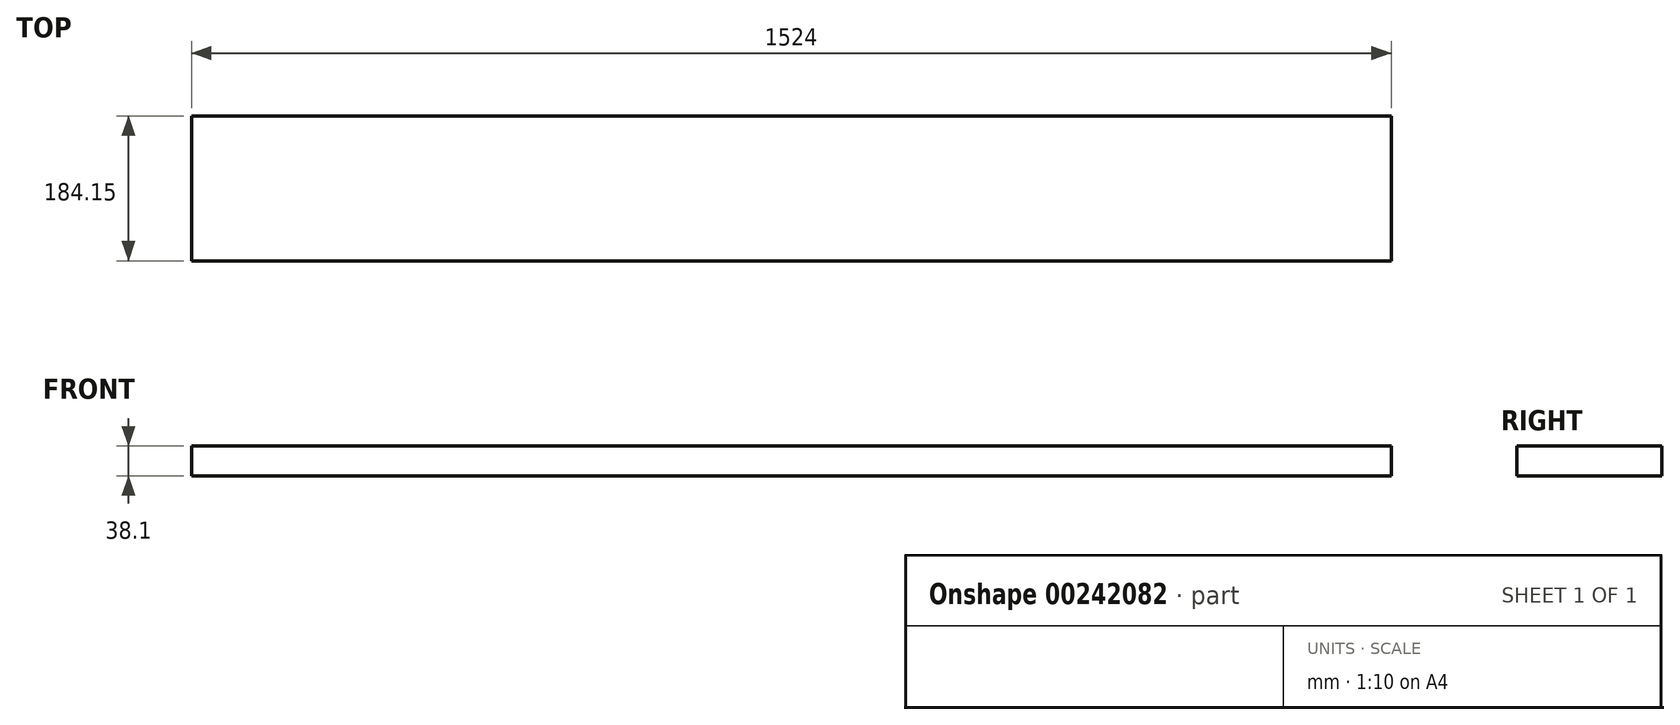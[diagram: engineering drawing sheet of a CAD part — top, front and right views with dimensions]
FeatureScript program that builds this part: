
annotation { "Feature Type Name" : "Feature", "Feature Type Description" : "" }
export const myFeature = defineFeature(function(context is Context, id is Id, definition is map)
    precondition{}
    {
        {
            var Q0;
            Q0=qCreatedBy(makeId("Top.planeOp"),FACE);
            var sketch = newSketch(context, id + "F0", { "sketchPlane" : qUnion([Q0])});
            skLineSegment(sketch, "E0.bottom", {"start": v(-253.24, 131.07) * mm, "end": v(1270.76, 131.07) * mm});
            skLineSegment(sketch, "E0.top", {"start": v(-253.24, -53.08) * mm, "end": v(1270.76, -53.08) * mm});
            skLineSegment(sketch, "E0.left", {"start": v(-253.24, 131.07) * mm, "end": v(-253.24, -53.08) * mm});
            skLineSegment(sketch, "E0.right", {"start": v(1270.76, 131.07) * mm, "end": v(1270.76, -53.08) * mm});
            skSolve(sketch);
        }
        {
            var Q0;
            Q0=makeQuery(id+"F0.imprint","IMPRINT",FACE,{"disambiguationData":[TD([[makeQuery(id+"F0.imprint","IMPRINT",EDGE,{"derivedFrom":sQuery(id+"F0.wireOp",EDGE,"E0.bottom")}),-1.0]])]});
            extrude(context, id + "F1", {"entities" : qUnion([Q0]), "depth" : 38.1 * mm});
        }
    });
